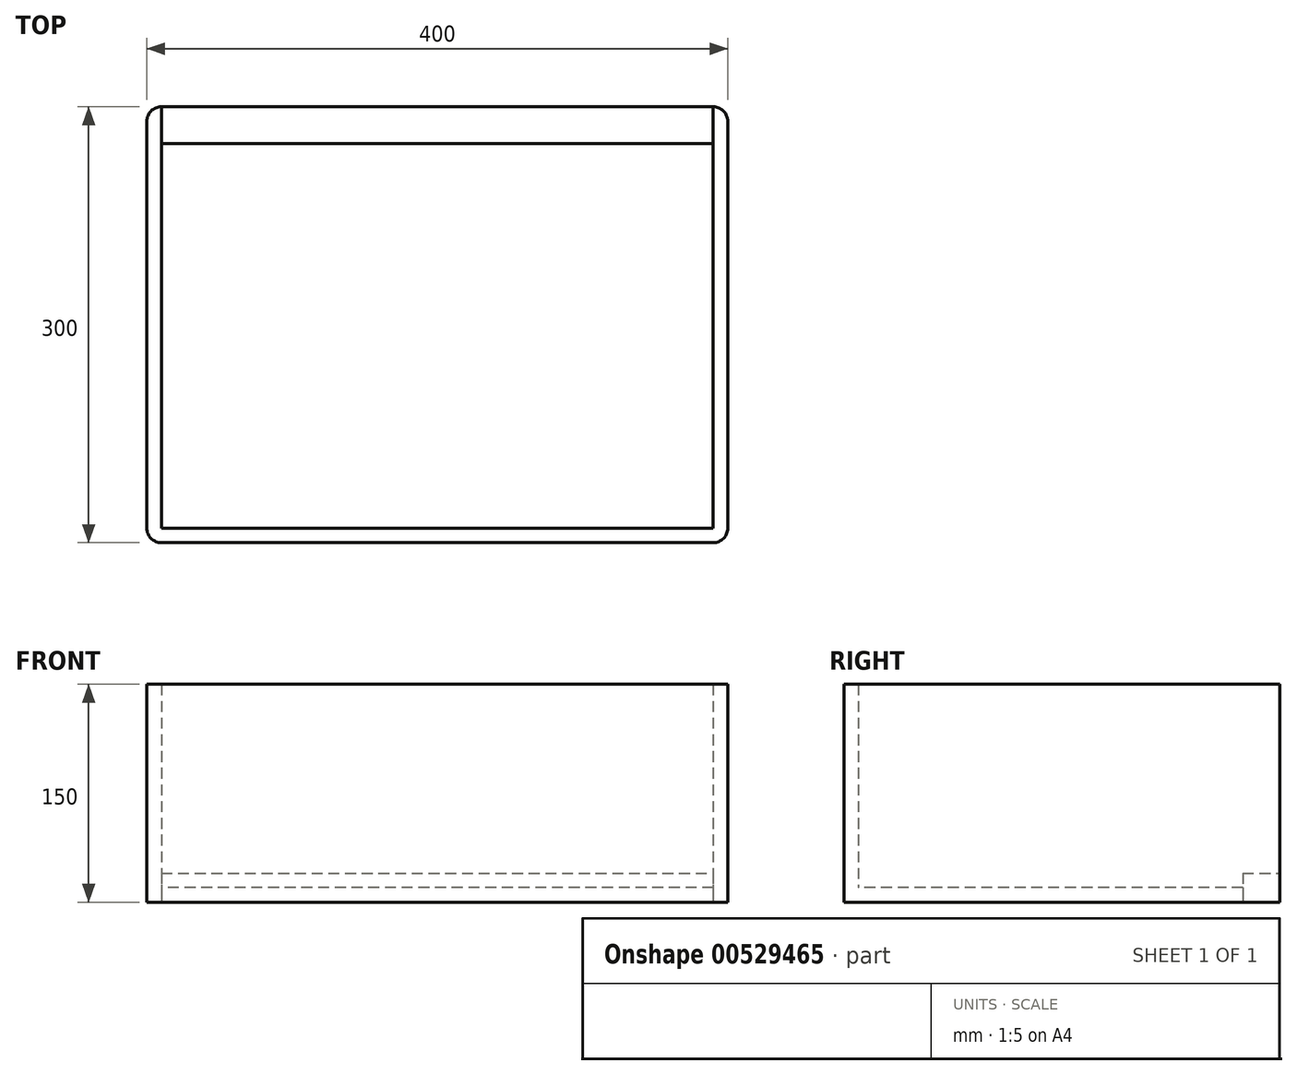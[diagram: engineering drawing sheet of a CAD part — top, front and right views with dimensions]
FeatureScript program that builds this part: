
annotation { "Feature Type Name" : "Feature", "Feature Type Description" : "" }
export const myFeature = defineFeature(function(context is Context, id is Id, definition is map)
    precondition{}
    {
        {
            var Q0;
            Q0=qCreatedBy(makeId("Top.planeOp"),FACE);
            var sketch = newSketch(context, id + "F0", { "sketchPlane" : qUnion([Q0])});
            skLineSegment(sketch, "E0.bottom", {"start": v(200, 150) * mm, "end": v(-200, 150) * mm});
            skLineSegment(sketch, "E0.top", {"start": v(200, -150) * mm, "end": v(-200, -150) * mm});
            skLineSegment(sketch, "E0.left", {"start": v(200, 150) * mm, "end": v(200, -150) * mm});
            skLineSegment(sketch, "E0.right", {"start": v(-200, 150) * mm, "end": v(-200, -150) * mm});
            skPoint(sketch, "E0.middle", {"position": v(0, 0) * mm});
            skSolve(sketch);
        }
        {
            var Q0;
            Q0=makeQuery(id+"F0.imprint","IMPRINT",FACE,{"disambiguationData":[TD([[makeQuery(id+"F0.imprint","IMPRINT",EDGE,{"derivedFrom":sQuery(id+"F0.wireOp",EDGE,"E0.bottom")}),1.0]])]});
            extrude(context, id + "F1", {"entities" : qUnion([Q0]), "endBound" : BoundingType.SYMMETRIC, "depth" : 150 * mm, "offsetDistance" : 25.4 * mm});
        }
        {
            var Q0;
            Q0=makeQuery(id+"F1.opExtrude","CAP_FACE",FACE,{"disambiguationData":[OSD([sQuery(id+"F0.wireOp",EDGE,"E0.bottom"),sQuery(id+"F0.wireOp",EDGE,"E0.top"),sQuery(id+"F0.wireOp",EDGE,"E0.left"),sQuery(id+"F0.wireOp",EDGE,"E0.right")])],"isStart":false});
            shell(context, id + "F2", {"entities" : qUnion([Q0]), "thickness" : 10 * mm});
        }
        {
            var Q0;
            Q0=makeQuery(id+"F1.opExtrude","SWEPT_EDGE",EDGE,{"disambiguationData":[OSD([sQuery(id+"F0.wireOp",EDGE,"E0.bottom"),sQuery(id+"F0.wireOp",EDGE,"E0.right")])]});
            var Q1;
            Q1=makeQuery(id+"F1.opExtrude","SWEPT_EDGE",EDGE,{"disambiguationData":[OSD([sQuery(id+"F0.wireOp",EDGE,"E0.bottom"),sQuery(id+"F0.wireOp",EDGE,"E0.left")])]});
            fillet(context, id + "F3", {"entities" : qUnion([Q0, Q1]), "radius" : 10 * mm, "tangentPropagation" : true, "allowEdgeOverflow" : false});
        }
        {
            var Q0;
            Q0=makeQuery(id+"F1.opExtrude","SWEPT_EDGE",EDGE,{"disambiguationData":[OSD([sQuery(id+"F0.wireOp",EDGE,"E0.top"),sQuery(id+"F0.wireOp",EDGE,"E0.left")])]});
            var Q1;
            Q1=makeQuery(id+"F1.opExtrude","SWEPT_EDGE",EDGE,{"disambiguationData":[OSD([sQuery(id+"F0.wireOp",EDGE,"E0.top"),sQuery(id+"F0.wireOp",EDGE,"E0.right")])]});
            fillet(context, id + "F4", {"entities" : qUnion([Q0, Q1]), "radius" : 10 * mm, "tangentPropagation" : true, "allowEdgeOverflow" : false});
        }
        {
            var Q0;
            Q0=makeQuery(id+"F1.opExtrude","SWEPT_FACE",FACE,{"disambiguationData":[OSD([sQuery(id+"F0.wireOp",EDGE,"E0.bottom")])]});
            extrude(context, id + "F5", {"entities" : qUnion([Q0]), "operationType" : NewBodyOperationType.REMOVE, "oppositeDirection" : true, "depth" : 25.4 * mm, "offsetDistance" : 25.4 * mm});
        }
        {
            var Q0;
            Q0=makeQuery(id+"F2.opShell","OFFSET_FACE",FACE,{"disambiguationData":[OSD([sQuery(id+"F0.wireOp",EDGE,"E0.bottom"),sQuery(id+"F0.wireOp",EDGE,"E0.top"),sQuery(id+"F0.wireOp",EDGE,"E0.left"),sQuery(id+"F0.wireOp",EDGE,"E0.right")])]});
            var sketch = newSketch(context, id + "F6", { "sketchPlane" : qUnion([Q0])});
            skLineSegment(sketch, "E1.bottom", {"start": v(-190, 124.6) * mm, "end": v(190, 124.6) * mm});
            skLineSegment(sketch, "E1.top", {"start": v(-190, 150) * mm, "end": v(190, 150) * mm});
            skLineSegment(sketch, "E1.left", {"start": v(-190, 124.6) * mm, "end": v(-190, 150) * mm});
            skLineSegment(sketch, "E1.right", {"start": v(190, 124.6) * mm, "end": v(190, 150) * mm});
            skSolve(sketch);
        }
        {
            var Q0;
            Q0=makeQuery(id+"F6.imprint","IMPRINT",FACE,{"disambiguationData":[TD([[makeQuery(id+"F6.imprint","IMPRINT",EDGE,{"derivedFrom":sQuery(id+"F6.wireOp",EDGE,"E1.bottom")}),1.0]])]});
            extrude(context, id + "F7", {"entities" : qUnion([Q0]), "endBound" : BoundingType.SYMMETRIC, "depth" : 20 * mm, "offsetDistance" : 25.4 * mm});
        }
    });
